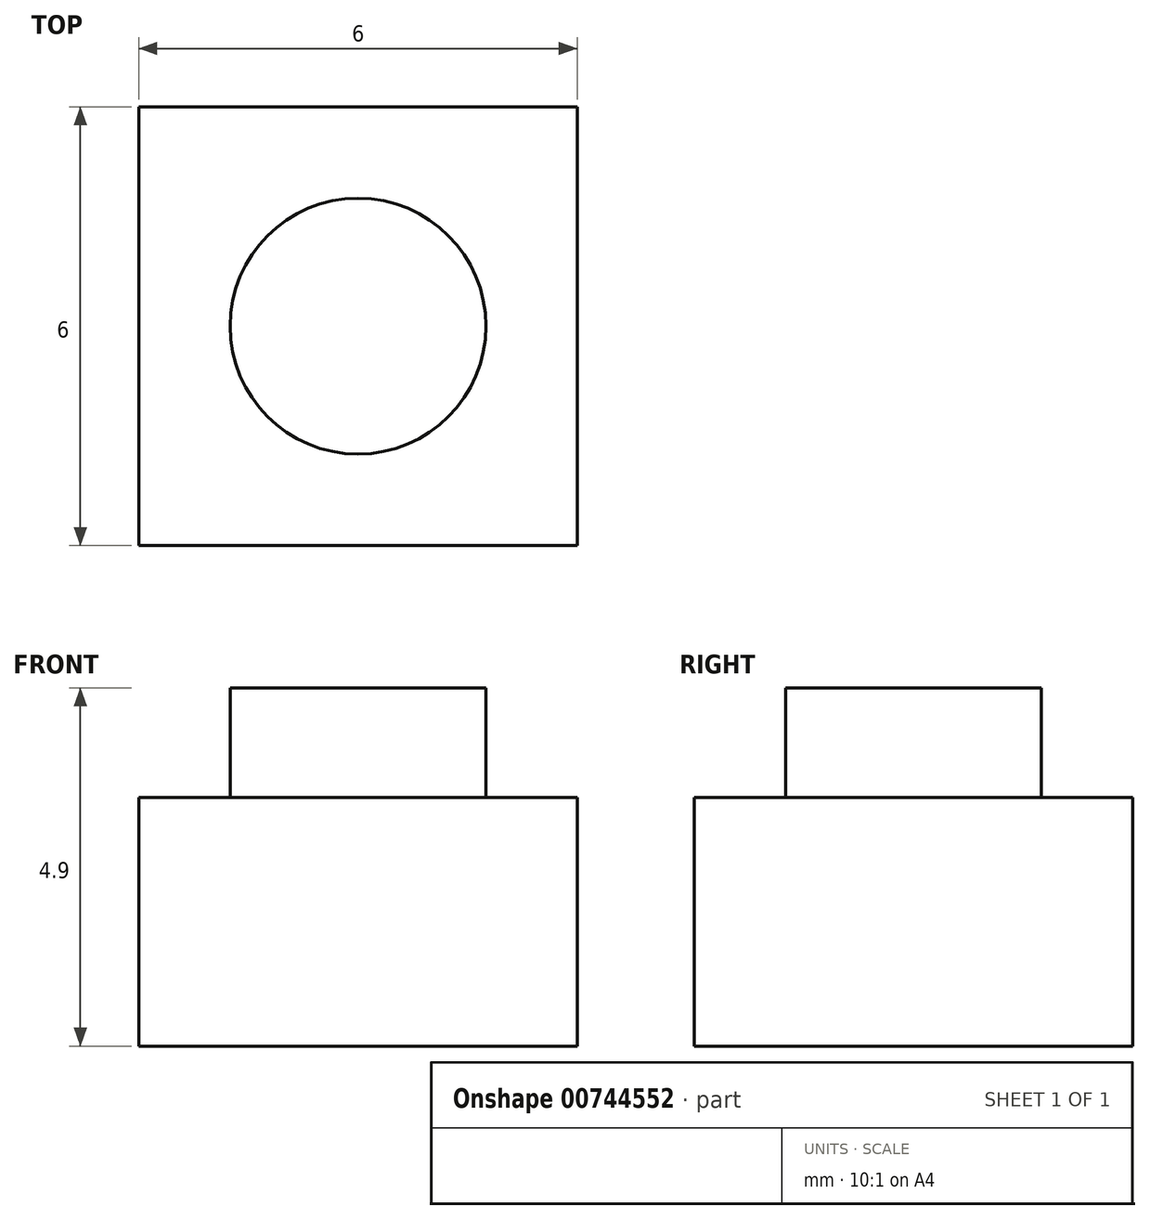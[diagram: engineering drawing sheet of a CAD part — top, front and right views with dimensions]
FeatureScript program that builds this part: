
annotation { "Feature Type Name" : "Feature", "Feature Type Description" : "" }
export const myFeature = defineFeature(function(context is Context, id is Id, definition is map)
    precondition{}
    {
        {
            var Q0;
            Q0=qCreatedBy(makeId("Top.planeOp"),FACE);
            var sketch = newSketch(context, id + "F0", { "sketchPlane" : qUnion([Q0])});
            skLineSegment(sketch, "E0.bottom", {"start": v(-3, 3) * mm, "end": v(3, 3) * mm});
            skLineSegment(sketch, "E0.top", {"start": v(-3, -3) * mm, "end": v(3, -3) * mm});
            skLineSegment(sketch, "E0.left", {"start": v(-3, 3) * mm, "end": v(-3, -3) * mm});
            skLineSegment(sketch, "E0.right", {"start": v(3, 3) * mm, "end": v(3, -3) * mm});
            skLineSegment(sketch, "E1", {"start": v(0, 0) * mm, "end": v(0, 6.84) * mm, "construction": true});
            skLineSegment(sketch, "E2", {"start": v(0, 0) * mm, "end": v(-5.32, 0) * mm, "construction": true});
            skSolve(sketch);
        }
        {
            var Q0;
            Q0 = qSketchRegion(id + "F0", true);
            extrude(context, id + "F1", {"entities" : qUnion([Q0]), "depth" : 3.4 * mm, "offsetDistance" : 25 * mm});
        }
        {
            var Q0;
            Q0=makeQuery(id+"F1.opExtrude","CAP_FACE",FACE,{"disambiguationData":[OSD([sQuery(id+"F0.wireOp",EDGE,"E0.bottom"),sQuery(id+"F0.wireOp",EDGE,"E0.top"),sQuery(id+"F0.wireOp",EDGE,"E0.left"),sQuery(id+"F0.wireOp",EDGE,"E0.right")])],"isStart":false});
            var sketch = newSketch(context, id + "F2", { "sketchPlane" : qUnion([Q0])});
            skCircle(sketch, "E3", {"center": v(0, 0) * mm, "radius": 1.75 * mm});
            skSolve(sketch);
        }
        {
            var Q0;
            Q0=makeQuery(id+"F2.imprint","IMPRINT",FACE,{"disambiguationData":[TD([[makeQuery(id+"F2.imprint","IMPRINT",EDGE,{"derivedFrom":sQuery(id+"F2.wireOp",EDGE,"E3")}),1.0]])]});
            extrude(context, id + "F3", {"entities" : qUnion([Q0]), "operationType" : NewBodyOperationType.ADD, "depth" : 1.5 * mm, "offsetDistance" : 25 * mm});
        }
    });
